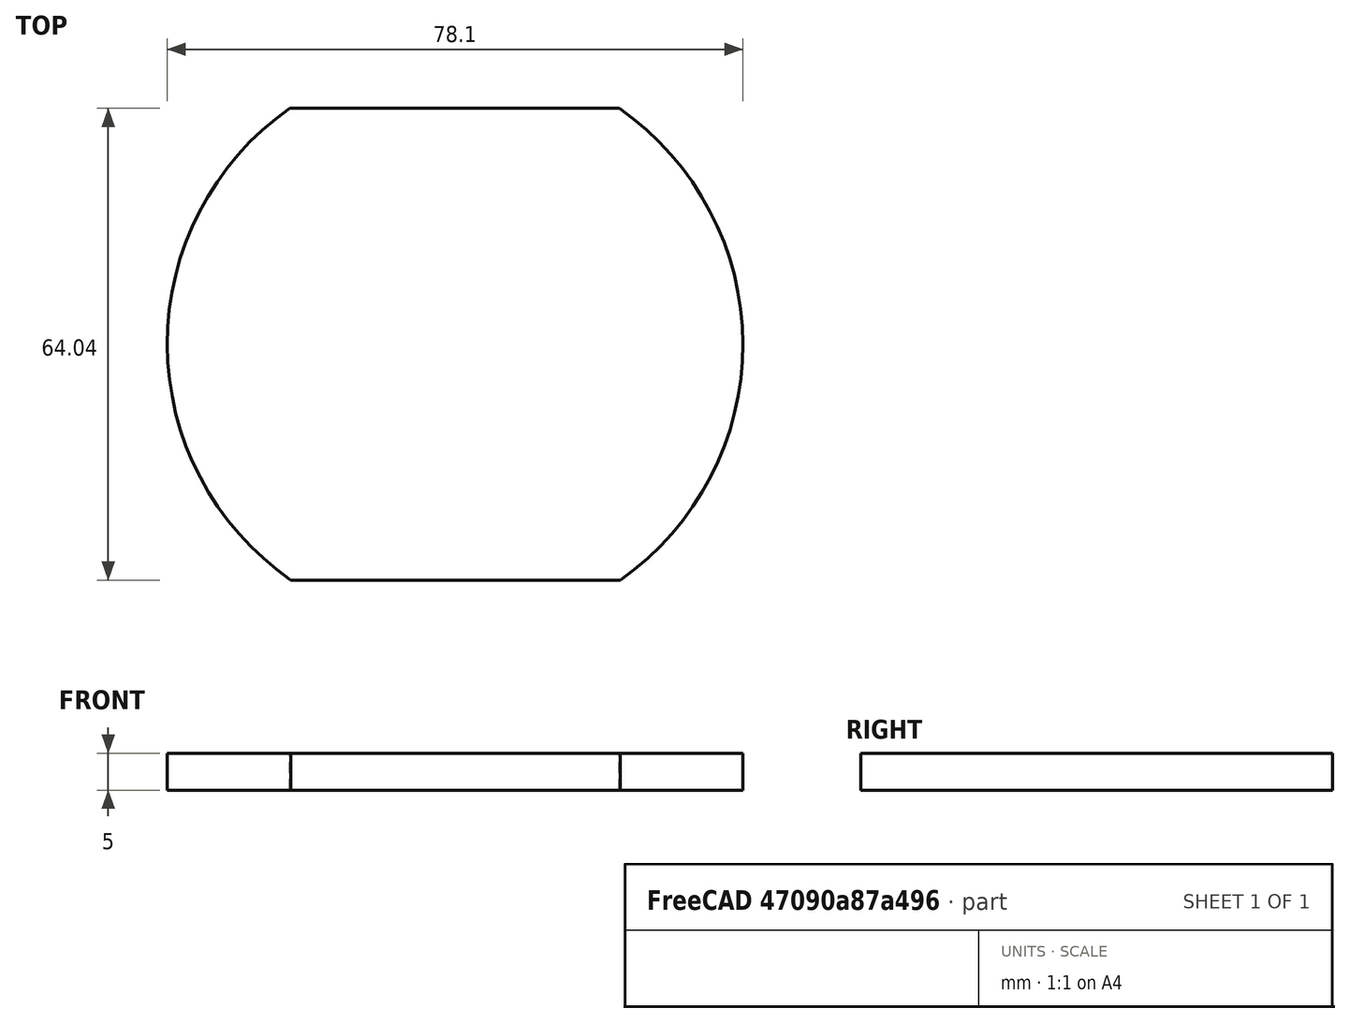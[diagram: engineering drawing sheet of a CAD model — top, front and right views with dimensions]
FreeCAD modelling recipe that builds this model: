
FCSTD DOCUMENT  (FreeCAD 1.0R39319 (Git))
Label: chord_cut_pattern_test
License: All rights reserved
LicenseURL: https://en.wikipedia.org/wiki/All_rights_reserved
objects: Sketcher::SketchObject×1, PartDesign::Pad×1, PartDesign::Body×1
note: 6 computed .brp shape members not serialized (recipe doc carries the construction recipe); baked Part::Feature solids carry a one-line shape summary decoded from their .brp

FEATURE [Sketcher::SketchObject] Sketch_1
  ArcFitTolerance = 1e-06
  AttachmentSupport = -> [XY_Plane]
  FullyConstrained = false
  MakeInternals = false
  MapMode = 5
  sketch-geometry (4):
    g0: ArcOfCircle CenterX=-0.00134139 CenterY=-7.04808 CenterZ=0 NormalX=0 NormalY=0 NormalZ=1 AngleXU=0 Radius=39.0492 StartAngle=5.32437 EndAngle=7.24728
    g1: LineSegment StartX=22.263 StartY=25.0321 StartZ=0 EndX=-22.4327 EndY=25.0321 EndZ=0
    g2: ArcOfCircle CenterX=0.00211253 CenterY=-6.92989 CenterZ=0 NormalX=0 NormalY=0 NormalZ=1 AngleXU=0 Radius=39.0499 StartAngle=2.18281 EndAngle=4.10567
    g3: LineSegment StartX=-22.263 StartY=-39.0104 StartZ=0 EndX=22.4319 EndY=-39.0104 EndZ=0
  constraints (7):
    c: Coincident(g0,g1)
    c: Coincident(g1,g2)
    c: Coincident(g2,g3)
    c: Coincident(g3,g0)
    c: Parallel(g1,g3)
    c: Horizontal(g1)
    c: Distance(g1,g3) = 78
FEATURE [PartDesign::Pad] Pad_1
  Direction = (0,0,1)
  Length = 5
  Length2 = 10
  Profile = -> Sketch_1
  Refine = true
  Suppressed = false
  Type = 0
FEATURE [PartDesign::Body] Body
  AllowCompound = false
  Group = -> [Sketch_1,Pad_1]
  Origin = -> Origin
  Tip = -> Pad_1
